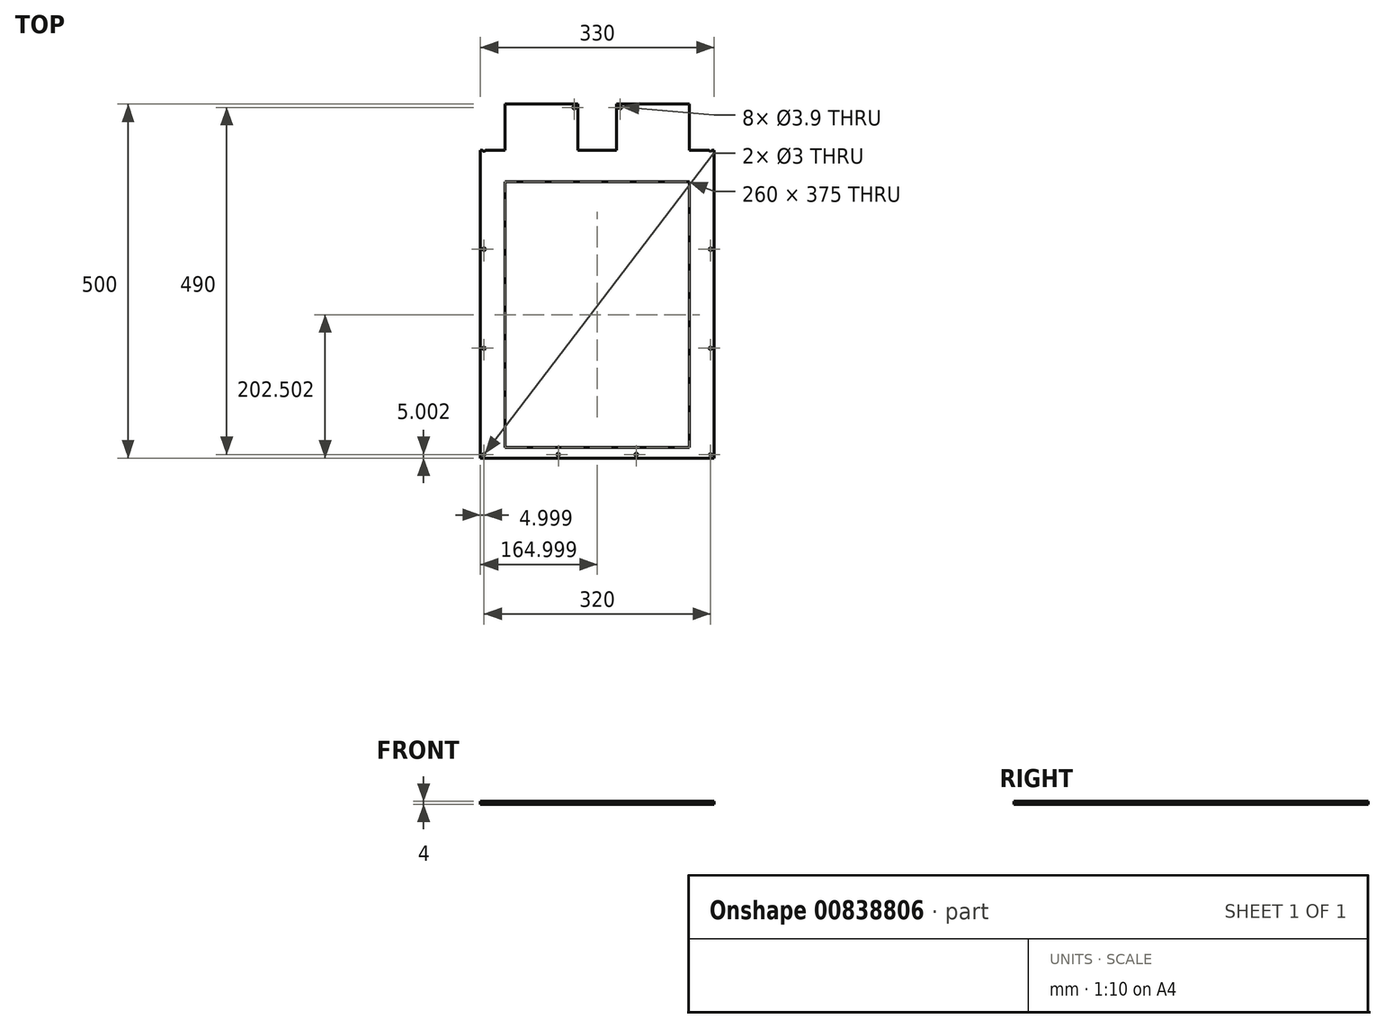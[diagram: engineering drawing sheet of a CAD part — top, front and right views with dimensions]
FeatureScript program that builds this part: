
annotation { "Feature Type Name" : "Feature", "Feature Type Description" : "" }
export const myFeature = defineFeature(function(context is Context, id is Id, definition is map)
    precondition{}
    {
        {
            var Q0;
            Q0=qCreatedBy(makeId("Top.planeOp"),FACE);
            var sketch = newSketch(context, id + "F0", { "sketchPlane" : qUnion([Q0])});
            skLineSegment(sketch, "E0.bottom", {"start": v(-158.26, -228.93) * mm, "end": v(171.74, -228.93) * mm});
            skLineSegment(sketch, "E0.top", {"start": v(-158.26, 271.07) * mm, "end": v(171.74, 271.07) * mm});
            skLineSegment(sketch, "E0.left", {"start": v(-158.26, -228.93) * mm, "end": v(-158.26, 271.07) * mm});
            skLineSegment(sketch, "E0.right", {"start": v(171.74, -228.93) * mm, "end": v(171.74, 271.07) * mm});
            skLineSegment(sketch, "E1", {"start": v(-123.26, 271.07) * mm, "end": v(-123.26, -228.93) * mm});
            skLineSegment(sketch, "E2", {"start": v(136.74, -228.93) * mm, "end": v(136.74, 271.07) * mm});
            skLineSegment(sketch, "E3.bottom", {"start": v(-158.26, 271.07) * mm, "end": v(-20.76, 271.07) * mm});
            skLineSegment(sketch, "E3.top", {"start": v(-158.26, 206.07) * mm, "end": v(-20.76, 206.07) * mm});
            skLineSegment(sketch, "E3.left", {"start": v(-158.26, 271.07) * mm, "end": v(-158.26, 206.07) * mm});
            skLineSegment(sketch, "E3.right", {"start": v(-20.76, 271.07) * mm, "end": v(-20.76, 206.07) * mm});
            skLineSegment(sketch, "E4.bottom", {"start": v(171.74, 271.07) * mm, "end": v(34.24, 271.07) * mm});
            skLineSegment(sketch, "E4.top", {"start": v(171.74, 206.07) * mm, "end": v(34.24, 206.07) * mm});
            skLineSegment(sketch, "E4.left", {"start": v(171.74, 271.07) * mm, "end": v(171.74, 206.07) * mm});
            skLineSegment(sketch, "E4.right", {"start": v(34.24, 271.07) * mm, "end": v(34.24, 206.07) * mm});
            skLineSegment(sketch, "E5", {"start": v(-158.26, -213.93) * mm, "end": v(171.74, -213.93) * mm});
            skLineSegment(sketch, "E6.top", {"start": v(171.74, 258.07) * mm, "end": v(155.74, 258.07) * mm, "construction": true});
            skLineSegment(sketch, "E6.right", {"start": v(155.74, 271.07) * mm, "end": v(155.74, 258.07) * mm, "construction": true});
            skLineSegment(sketch, "E7.top", {"start": v(-158.26, 258.07) * mm, "end": v(-142.26, 258.07) * mm, "construction": true});
            skLineSegment(sketch, "E7.right", {"start": v(-142.26, 271.07) * mm, "end": v(-142.26, 258.07) * mm, "construction": true});
            skCircle(sketch, "E8", {"center": v(-142.26, 258.07) * mm, "radius": 7.48 * mm});
            skCircle(sketch, "E9", {"center": v(155.74, 258.07) * mm, "radius": 7.48 * mm});
            skLineSegment(sketch, "E10.top", {"start": v(-158.26, 266.07) * mm, "end": v(-153.26, 266.07) * mm, "construction": true});
            skLineSegment(sketch, "E10.right", {"start": v(-153.26, 271.07) * mm, "end": v(-153.26, 266.07) * mm, "construction": true});
            skCircle(sketch, "E11", {"center": v(-153.26, 266.07) * mm, "radius": 1.5 * mm});
            skLineSegment(sketch, "E12.top", {"start": v(-158.26, -223.93) * mm, "end": v(-153.26, -223.93) * mm, "construction": true});
            skLineSegment(sketch, "E12.right", {"start": v(-153.26, -228.93) * mm, "end": v(-153.26, -223.93) * mm, "construction": true});
            skCircle(sketch, "E13", {"center": v(-153.26, -223.93) * mm, "radius": 1.5 * mm});
            skLineSegment(sketch, "E14.top", {"start": v(171.74, -223.93) * mm, "end": v(166.74, -223.93) * mm, "construction": true});
            skLineSegment(sketch, "E14.right", {"start": v(166.74, -228.93) * mm, "end": v(166.74, -223.93) * mm, "construction": true});
            skCircle(sketch, "E15", {"center": v(166.74, -223.93) * mm, "radius": 1.5 * mm});
            skLineSegment(sketch, "E16.top", {"start": v(171.74, 266.07) * mm, "end": v(166.74, 266.07) * mm, "construction": true});
            skLineSegment(sketch, "E16.right", {"start": v(166.74, 271.07) * mm, "end": v(166.74, 266.07) * mm, "construction": true});
            skCircle(sketch, "E17", {"center": v(166.74, 266.07) * mm, "radius": 1.5 * mm});
            skLineSegment(sketch, "E18.bottom", {"start": v(-20.76, 271.07) * mm, "end": v(-25.76, 271.07) * mm, "construction": true});
            skLineSegment(sketch, "E18.top", {"start": v(-20.76, 266.07) * mm, "end": v(-25.76, 266.07) * mm, "construction": true});
            skLineSegment(sketch, "E18.left", {"start": v(-20.76, 271.07) * mm, "end": v(-20.76, 266.07) * mm, "construction": true});
            skLineSegment(sketch, "E18.right", {"start": v(-25.76, 271.07) * mm, "end": v(-25.76, 266.07) * mm, "construction": true});
            skLineSegment(sketch, "E19.bottom", {"start": v(34.24, 271.07) * mm, "end": v(39.24, 271.07) * mm, "construction": true});
            skLineSegment(sketch, "E19.top", {"start": v(34.24, 266.07) * mm, "end": v(39.24, 266.07) * mm, "construction": true});
            skLineSegment(sketch, "E19.left", {"start": v(34.24, 271.07) * mm, "end": v(34.24, 266.07) * mm, "construction": true});
            skLineSegment(sketch, "E19.right", {"start": v(39.24, 271.07) * mm, "end": v(39.24, 266.07) * mm, "construction": true});
            skCircle(sketch, "E20", {"center": v(-25.76, 266.07) * mm, "radius": 1.95 * mm});
            skCircle(sketch, "E21", {"center": v(39.24, 266.07) * mm, "radius": 1.95 * mm});
            skLineSegment(sketch, "E22.top", {"start": v(-48.26, -223.93) * mm, "end": v(61.74, -223.93) * mm, "construction": true});
            skLineSegment(sketch, "E22.left", {"start": v(-48.26, -228.93) * mm, "end": v(-48.26, -223.93) * mm, "construction": true});
            skLineSegment(sketch, "E22.right", {"start": v(61.74, -228.93) * mm, "end": v(61.74, -223.93) * mm, "construction": true});
            skCircle(sketch, "E23", {"center": v(-48.26, -223.93) * mm, "radius": 1.95 * mm});
            skCircle(sketch, "E24", {"center": v(61.74, -223.93) * mm, "radius": 1.95 * mm});
            skLineSegment(sketch, "E25", {"start": v(-158.26, -213.93) * mm, "end": v(-158.26, -73.93) * mm, "construction": true});
            skLineSegment(sketch, "E26", {"start": v(-158.26, -73.93) * mm, "end": v(-158.26, 66.07) * mm, "construction": true});
            skLineSegment(sketch, "E27", {"start": v(-153.26, 266.07) * mm, "end": v(-153.26, -223.93) * mm, "construction": true});
            skLineSegment(sketch, "E28", {"start": v(-158.26, -73.93) * mm, "end": v(-153.26, -73.93) * mm, "construction": true});
            skLineSegment(sketch, "E29", {"start": v(-158.26, 66.07) * mm, "end": v(-153.26, 66.07) * mm, "construction": true});
            skLineSegment(sketch, "E30", {"start": v(-158.26, 206.07) * mm, "end": v(-153.26, 206.07) * mm, "construction": true});
            skCircle(sketch, "E31", {"center": v(-153.26, -73.93) * mm, "radius": 1.95 * mm});
            skCircle(sketch, "E32", {"center": v(-153.26, 66.07) * mm, "radius": 1.95 * mm});
            skCircle(sketch, "E33", {"center": v(-153.26, 206.07) * mm, "radius": 1.95 * mm});
            skLineSegment(sketch, "E34", {"start": v(171.74, -213.93) * mm, "end": v(171.74, -73.93) * mm, "construction": true});
            skLineSegment(sketch, "E35", {"start": v(171.74, -73.93) * mm, "end": v(171.74, 66.07) * mm, "construction": true});
            skLineSegment(sketch, "E36", {"start": v(166.74, 266.07) * mm, "end": v(166.74, -223.93) * mm, "construction": true});
            skLineSegment(sketch, "E37", {"start": v(171.74, -73.93) * mm, "end": v(166.74, -73.93) * mm, "construction": true});
            skLineSegment(sketch, "E38", {"start": v(171.74, 66.07) * mm, "end": v(166.74, 66.07) * mm, "construction": true});
            skLineSegment(sketch, "E39", {"start": v(171.74, 258.07) * mm, "end": v(166.74, 258.07) * mm, "construction": true});
            skLineSegment(sketch, "E40", {"start": v(171.74, 206.07) * mm, "end": v(166.74, 206.07) * mm, "construction": true});
            skCircle(sketch, "E41", {"center": v(166.74, 206.07) * mm, "radius": 1.95 * mm});
            skCircle(sketch, "E42", {"center": v(166.74, 66.07) * mm, "radius": 1.95 * mm});
            skCircle(sketch, "E43", {"center": v(166.74, -73.93) * mm, "radius": 1.95 * mm});
            skLineSegment(sketch, "E44", {"start": v(-123.26, 206.07) * mm, "end": v(-123.26, 161.07) * mm, "construction": true});
            skLineSegment(sketch, "E45", {"start": v(136.74, 206.07) * mm, "end": v(136.74, 161.07) * mm, "construction": true});
            skLineSegment(sketch, "E46", {"start": v(136.74, 161.07) * mm, "end": v(-123.26, 161.07) * mm});
            skLineSegment(sketch, "E47", {"start": v(-20.76, 206.07) * mm, "end": v(34.24, 206.07) * mm});
            skSolve(sketch);
        }
        {
            var Q0;
            {var subQ5=sQuery(id+"F0.wireOp",EDGE,"E3.right");Q0=makeQuery(id+"F0.imprint","IMPRINT",FACE,{"disambiguationData":[TD([[makeQuery(id+"F0.imprint","IMPRINT",EDGE,{"derivedFrom":subQ5}),-1.0]])]});}
            var Q1;
            {var subQ5=sQuery(id+"F0.wireOp",EDGE,"E3.left");Q1=makeQuery(id+"F0.imprint","IMPRINT",FACE,{"disambiguationData":[TD([[makeQuery(id+"F0.imprint","IMPRINT",EDGE,{"derivedFrom":subQ5}),1.0]])]});}
            var Q2;
            {var subQ0=sQuery(id+"F0.wireOp",EDGE,"E3.top");var subQ5=sQuery(id+"F0.wireOp",EDGE,"E1");var subQ6=makeQuery(id+"F0.imprint","INTERSECT",VERTEX,{"derivedFrom":[subQ5,subQ0]});Q2=makeQuery(id+"F0.imprint","IMPRINT",FACE,{"disambiguationData":[TD([[makeQuery(id+"F0.imprint","IMPRINT",EDGE,{"disambiguationData":[TD([[subQ6,-1.0]])],"derivedFrom":subQ5}),-1.0]])]});}
            var Q3;
            {var subQ0=sQuery(id+"F0.wireOp",EDGE,"E0.left");var subQ1=sQuery(id+"F0.wireOp",EDGE,"E0.bottom");var subQ2=makeQuery(id+"F0.imprint","INTERSECT",VERTEX,{"derivedFrom":[subQ1,subQ0]});Q3=makeQuery(id+"F0.imprint","IMPRINT",FACE,{"disambiguationData":[TD([[makeQuery(id+"F0.imprint","IMPRINT",EDGE,{"disambiguationData":[TD([[subQ2,-1.0]])],"derivedFrom":subQ1}),1.0]])]});}
            var Q4;
            {var subQ0=sQuery(id+"F0.wireOp",EDGE,"E1");var subQ1=sQuery(id+"F0.wireOp",EDGE,"E0.bottom");var subQ2=makeQuery(id+"F0.imprint","INTERSECT",VERTEX,{"derivedFrom":[subQ1,subQ0]});Q4=makeQuery(id+"F0.imprint","IMPRINT",FACE,{"disambiguationData":[TD([[makeQuery(id+"F0.imprint","IMPRINT",EDGE,{"disambiguationData":[TD([[subQ2,-1.0]])],"derivedFrom":subQ1}),1.0]])]});}
            var Q5;
            {var subQ0=sQuery(id+"F0.wireOp",EDGE,"E0.right");var subQ1=sQuery(id+"F0.wireOp",EDGE,"E0.bottom");var subQ2=makeQuery(id+"F0.imprint","INTERSECT",VERTEX,{"derivedFrom":[subQ1,subQ0]});Q5=makeQuery(id+"F0.imprint","IMPRINT",FACE,{"disambiguationData":[TD([[makeQuery(id+"F0.imprint","IMPRINT",EDGE,{"disambiguationData":[TD([[subQ2,1.0]])],"derivedFrom":subQ1}),1.0]])]});}
            var Q6;
            {var subQ3=sQuery(id+"F0.wireOp",EDGE,"E5");var subQ5=sQuery(id+"F0.wireOp",EDGE,"E2");var subQ6=makeQuery(id+"F0.imprint","INTERSECT",VERTEX,{"derivedFrom":[subQ5,subQ3]});Q6=makeQuery(id+"F0.imprint","IMPRINT",FACE,{"disambiguationData":[TD([[makeQuery(id+"F0.imprint","IMPRINT",EDGE,{"disambiguationData":[TD([[subQ6,-1.0]])],"derivedFrom":subQ5}),-1.0]])]});}
            var Q7;
            {var subQ5=sQuery(id+"F0.wireOp",EDGE,"E4.left");Q7=makeQuery(id+"F0.imprint","IMPRINT",FACE,{"disambiguationData":[TD([[makeQuery(id+"F0.imprint","IMPRINT",EDGE,{"derivedFrom":subQ5}),-1.0]])]});}
            var Q8;
            {var subQ5=sQuery(id+"F0.wireOp",EDGE,"E4.right");Q8=makeQuery(id+"F0.imprint","IMPRINT",FACE,{"disambiguationData":[TD([[makeQuery(id+"F0.imprint","IMPRINT",EDGE,{"derivedFrom":subQ5}),1.0]])]});}
            var Q9;
            {var subQ7=sQuery(id+"F0.wireOp",EDGE,"E46");Q9=makeQuery(id+"F0.imprint","IMPRINT",FACE,{"disambiguationData":[TD([[makeQuery(id+"F0.imprint","IMPRINT",EDGE,{"derivedFrom":subQ7}),-1.0]])]});}
            extrude(context, id + "F1", {"entities" : qUnion([Q0, Q1, Q2, Q3, Q4, Q5, Q6, Q7, Q8, Q9]), "depth" : 4 * mm, "offsetDistance" : 25 * mm});
        }
    });
